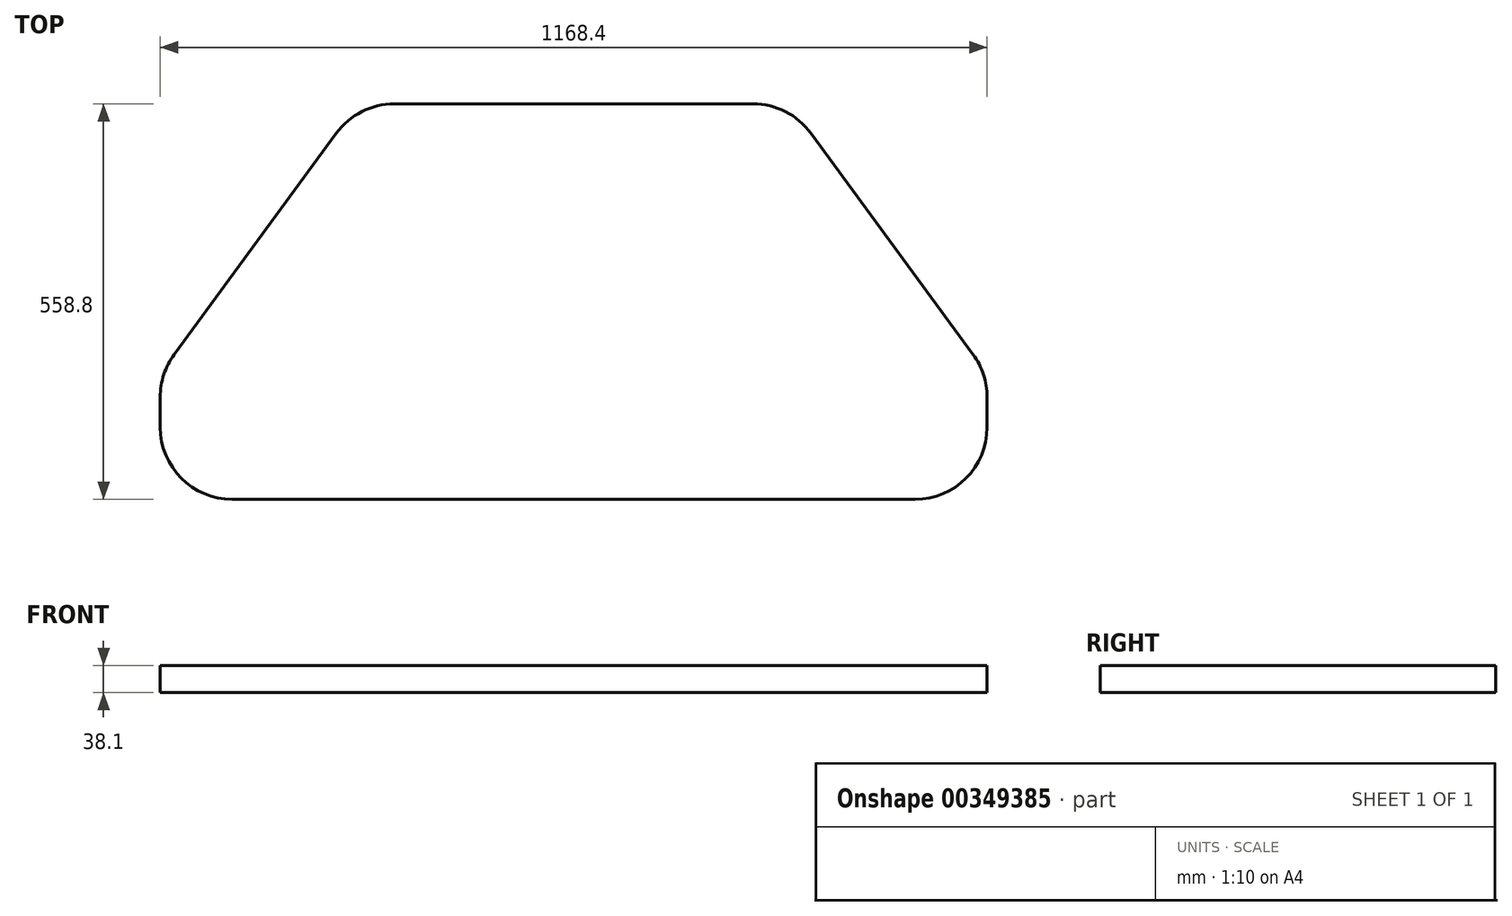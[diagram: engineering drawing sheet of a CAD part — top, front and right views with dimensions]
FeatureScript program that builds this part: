
annotation { "Feature Type Name" : "Feature", "Feature Type Description" : "" }
export const myFeature = defineFeature(function(context is Context, id is Id, definition is map)
    precondition{}
    {
        {
            var Q0;
            Q0=qCreatedBy(makeId("Top.planeOp"),FACE);
            var sketch = newSketch(context, id + "F0", { "sketchPlane" : qUnion([Q0])});
            skLineSegment(sketch, "E0", {"start": v(-586.55, -53.36) * mm, "end": v(581.85, -53.36) * mm});
            skLineSegment(sketch, "E1", {"start": v(-2.35, -53.36) * mm, "end": v(-2.35, 505.44) * mm, "construction": true});
            skLineSegment(sketch, "E2", {"start": v(-2.35, 505.44) * mm, "end": v(-307.15, 505.44) * mm});
            skLineSegment(sketch, "E3", {"start": v(-307.15, 505.44) * mm, "end": v(-586.55, 124.44) * mm});
            skLineSegment(sketch, "E4", {"start": v(-586.55, 124.44) * mm, "end": v(-586.55, -53.36) * mm});
            skLineSegment(sketch, "E5.MirrorCS", {"start": v(-2.35, 505.44) * mm, "end": v(302.45, 505.44) * mm});
            skLineSegment(sketch, "E6.MirrorCS", {"start": v(302.45, 505.44) * mm, "end": v(581.85, 124.44) * mm});
            skLineSegment(sketch, "E7.MirrorCS", {"start": v(581.85, 124.44) * mm, "end": v(581.85, -53.36) * mm});
            skSolve(sketch);
        }
        {
            var Q0;
            Q0=makeQuery(id+"F0.imprint","IMPRINT",FACE,{"disambiguationData":[TD([[makeQuery(id+"F0.imprint","IMPRINT",EDGE,{"derivedFrom":sQuery(id+"F0.wireOp",EDGE,"E0")}),1.0]])]});
            extrude(context, id + "F1", {"entities" : qUnion([Q0]), "depth" : 38.1 * mm});
        }
        {
            var Q0;
            Q0=makeQuery(id+"F1.opExtrude","SWEPT_EDGE",EDGE,{"disambiguationData":[OSD([sQuery(id+"F0.wireOp",EDGE,"E3"),sQuery(id+"F0.wireOp",EDGE,"E4")])]});
            var Q1;
            Q1=makeQuery(id+"F1.opExtrude","SWEPT_EDGE",EDGE,{"disambiguationData":[OSD([sQuery(id+"F0.wireOp",EDGE,"E2"),sQuery(id+"F0.wireOp",EDGE,"E3")])]});
            var Q2;
            Q2=makeQuery(id+"F1.opExtrude","SWEPT_EDGE",EDGE,{"disambiguationData":[OSD([sQuery(id+"F0.wireOp",EDGE,"E5.MirrorCS"),sQuery(id+"F0.wireOp",EDGE,"E6.MirrorCS")])]});
            var Q3;
            Q3=makeQuery(id+"F1.opExtrude","SWEPT_EDGE",EDGE,{"disambiguationData":[OSD([sQuery(id+"F0.wireOp",EDGE,"E6.MirrorCS"),sQuery(id+"F0.wireOp",EDGE,"E7.MirrorCS")])]});
            var Q4;
            Q4=makeQuery(id+"F1.opExtrude","SWEPT_EDGE",EDGE,{"disambiguationData":[OSD([sQuery(id+"F0.wireOp",EDGE,"E0"),sQuery(id+"F0.wireOp",EDGE,"E7.MirrorCS")])]});
            var Q5;
            Q5=makeQuery(id+"F1.opExtrude","SWEPT_EDGE",EDGE,{"disambiguationData":[OSD([sQuery(id+"F0.wireOp",EDGE,"E0"),sQuery(id+"F0.wireOp",EDGE,"E4")])]});
            fillet(context, id + "F2", {"entities" : qUnion([Q0, Q1, Q2, Q3, Q4, Q5]), "radius" : 101.6 * mm, "tangentPropagation" : true, "allowEdgeOverflow" : false});
        }
    });
